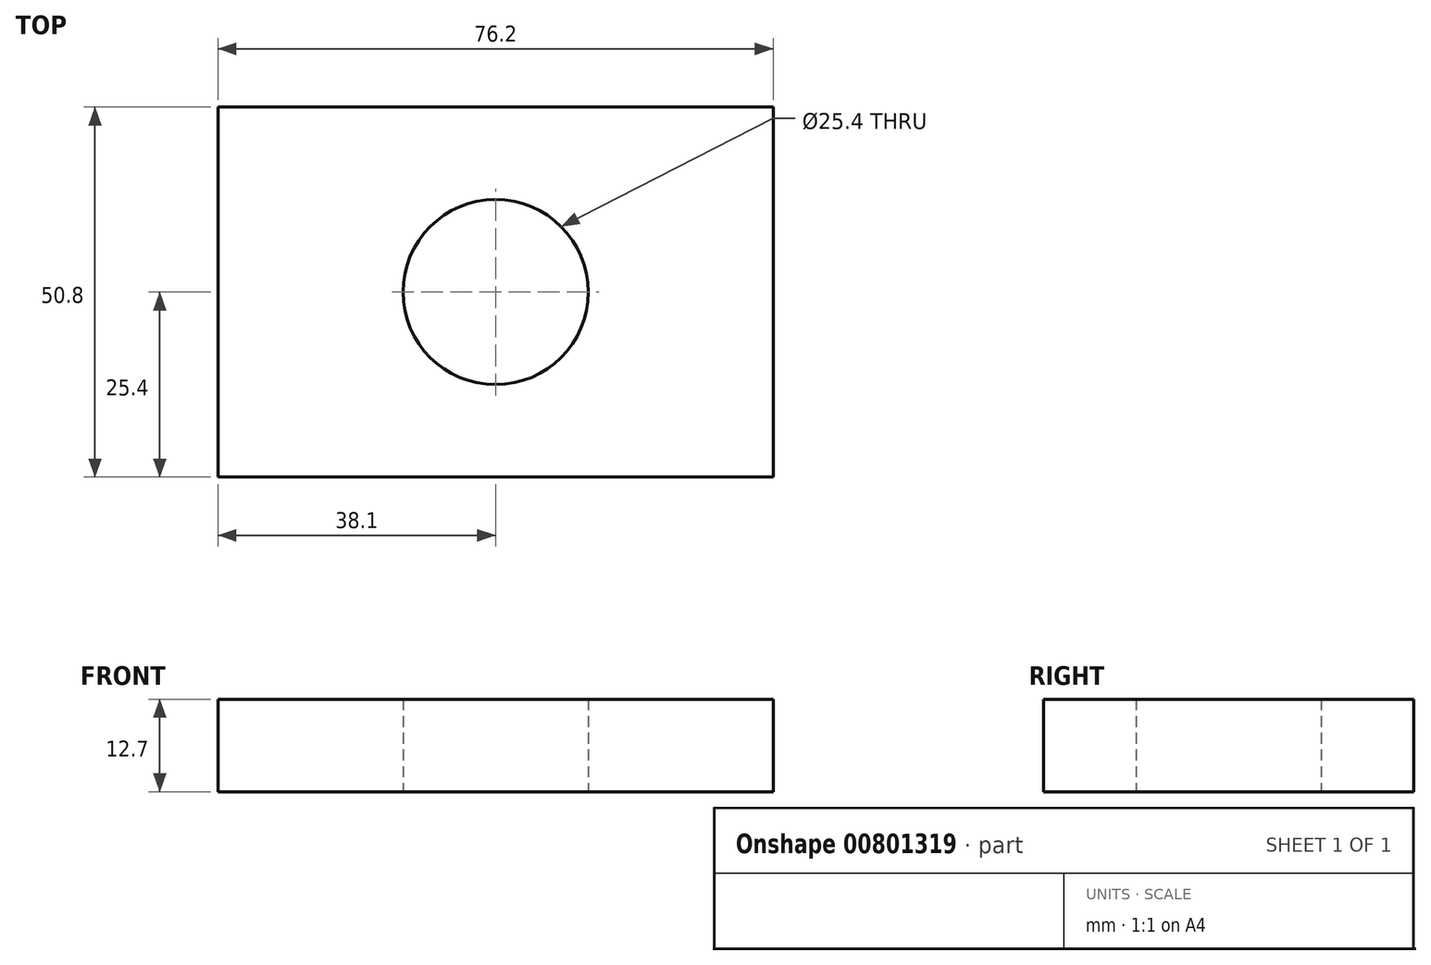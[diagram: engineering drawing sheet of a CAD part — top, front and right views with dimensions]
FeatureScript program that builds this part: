
annotation { "Feature Type Name" : "Feature", "Feature Type Description" : "" }
export const myFeature = defineFeature(function(context is Context, id is Id, definition is map)
    precondition{}
    {
        {
            var Q0;
            Q0=qCreatedBy(makeId("Top.planeOp"),FACE);
            var sketch = newSketch(context, id + "F0", { "sketchPlane" : qUnion([Q0])});
            skLineSegment(sketch, "E0.bottom", {"start": v(-38.1, 25.4) * mm, "end": v(38.1, 25.4) * mm});
            skLineSegment(sketch, "E0.top", {"start": v(-38.1, -25.4) * mm, "end": v(38.1, -25.4) * mm});
            skLineSegment(sketch, "E0.left", {"start": v(-38.1, 25.4) * mm, "end": v(-38.1, -25.4) * mm});
            skLineSegment(sketch, "E0.right", {"start": v(38.1, 25.4) * mm, "end": v(38.1, -25.4) * mm});
            skPoint(sketch, "E0.middle", {"position": v(0, 0) * mm});
            skCircle(sketch, "E1", {"center": v(0, 0) * mm, "radius": 12.7 * mm});
            skSolve(sketch);
        }
        {
            var Q0;
            Q0=makeQuery(id+"F0.imprint","IMPRINT",FACE,{"disambiguationData":[TD([[makeQuery(id+"F0.imprint","IMPRINT",EDGE,{"derivedFrom":sQuery(id+"F0.wireOp",EDGE,"E0.bottom")}),-1.0]])]});
            extrude(context, id + "F1", {"entities" : qUnion([Q0]), "depth" : 12.7 * mm, "offsetDistance" : 25.4 * mm});
        }
    });
